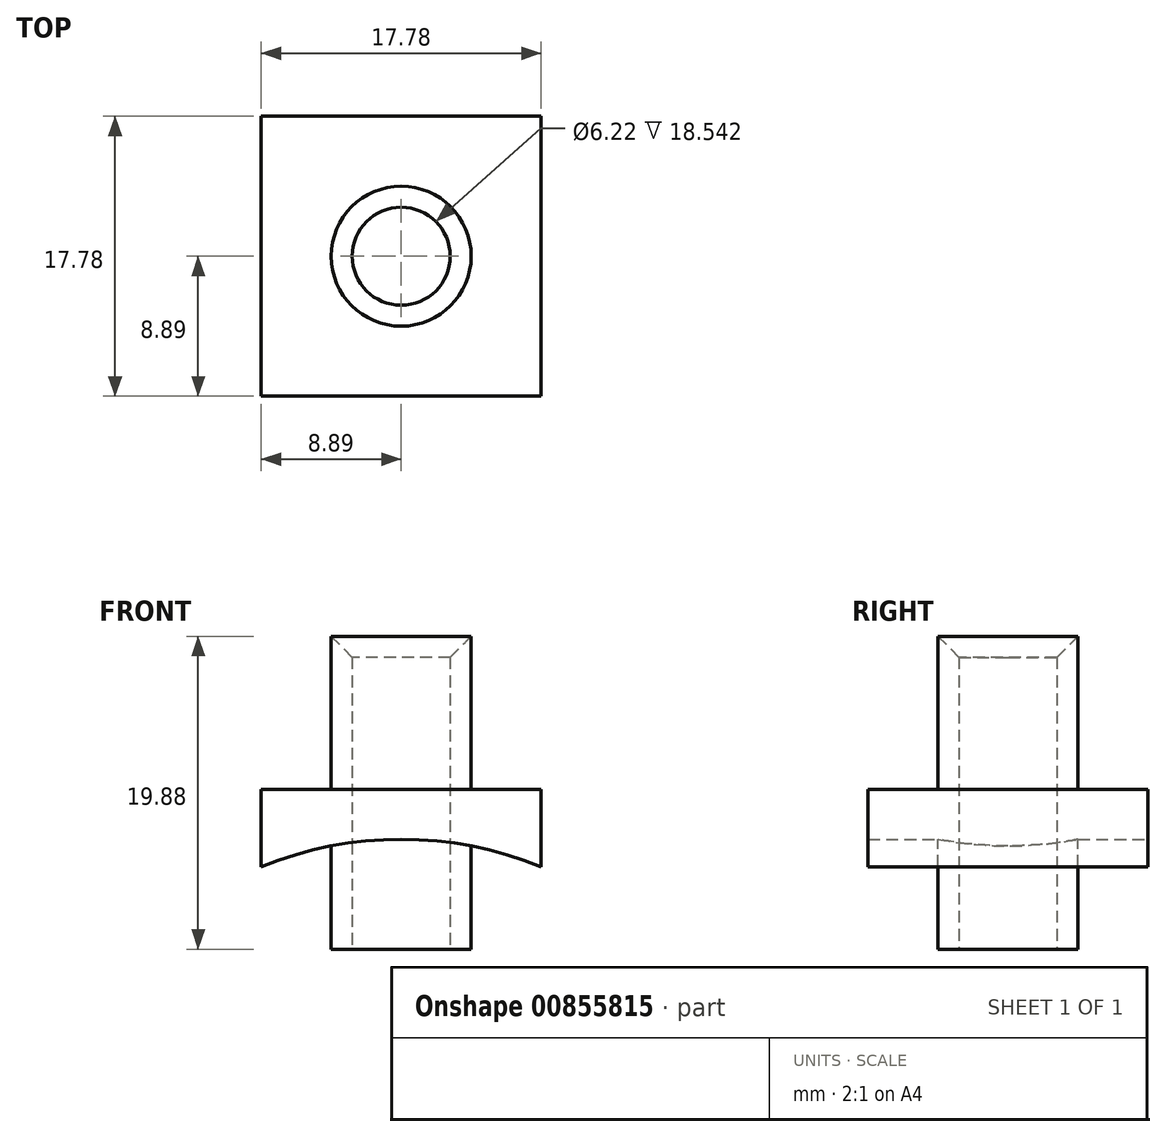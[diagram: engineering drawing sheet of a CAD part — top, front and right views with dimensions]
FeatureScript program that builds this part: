
annotation { "Feature Type Name" : "Feature", "Feature Type Description" : "" }
export const myFeature = defineFeature(function(context is Context, id is Id, definition is map)
    precondition{}
    {
        {
            var Q0;
            Q0=qCreatedBy(makeId("Top.planeOp"),FACE);
            var sketch = newSketch(context, id + "F0", { "sketchPlane" : qUnion([Q0])});
            skLineSegment(sketch, "E0.bottom", {"start": v(0, 17.78) * mm, "end": v(17.78, 17.78) * mm});
            skLineSegment(sketch, "E0.top", {"start": v(0, 0) * mm, "end": v(17.78, 0) * mm});
            skLineSegment(sketch, "E0.left", {"start": v(0, 17.78) * mm, "end": v(0, 0) * mm});
            skLineSegment(sketch, "E0.right", {"start": v(17.78, 17.78) * mm, "end": v(17.78, 0) * mm});
            skSolve(sketch);
        }
        {
            var Q0;
            Q0=makeQuery(id+"F0.imprint","IMPRINT",FACE,{"disambiguationData":[TD([[makeQuery(id+"F0.imprint","IMPRINT",EDGE,{"derivedFrom":sQuery(id+"F0.wireOp",EDGE,"E0.bottom")}),-1.0]])]});
            extrude(context, id + "F1", {"entities" : qUnion([Q0]), "depth" : 7.62 * mm, "offsetDistance" : 25.4 * mm});
        }
        {
            var Q0;
            Q0=makeQuery(id+"F1.opExtrude","CAP_FACE",FACE,{"disambiguationData":[OSD([sQuery(id+"F0.wireOp",EDGE,"E0.bottom"),sQuery(id+"F0.wireOp",EDGE,"E0.top"),sQuery(id+"F0.wireOp",EDGE,"E0.left"),sQuery(id+"F0.wireOp",EDGE,"E0.right")])],"isStart":true});
            cPlane(context, id + "F2", {"entities" : qUnion([Q0]), "cplaneType" : CPlaneType.OFFSET, "offset" : 19.05 * mm, "width" : 152.4 * mm, "height" : 152.4 * mm});
        }
        {
            var Q0;
            Q0=qCreatedBy(id+"F2.planeOp",FACE);
            var sketch = newSketch(context, id + "F3", { "sketchPlane" : qUnion([Q0])});
            skLineSegment(sketch, "E1.bottom", {"start": v(-9.53, 2.47) * mm, "end": v(-14.6, 2.47) * mm});
            skLineSegment(sketch, "E1.top", {"start": v(-9.52, -20.25) * mm, "end": v(-14.6, -20.25) * mm});
            skLineSegment(sketch, "E1.left", {"start": v(-9.53, 2.47) * mm, "end": v(-9.52, -20.25) * mm});
            skLineSegment(sketch, "E1.right", {"start": v(-14.6, 2.47) * mm, "end": v(-14.6, -20.25) * mm});
            skLineSegment(sketch, "E2", {"start": v(8.9, 0) * mm, "end": v(8.9, -24.22) * mm, "construction": true});
            skSolve(sketch);
        }
        {
            var Q0;
            Q0=makeQuery(id+"F3.imprint","IMPRINT",FACE,{"disambiguationData":[TD([[makeQuery(id+"F3.imprint","IMPRINT",EDGE,{"derivedFrom":sQuery(id+"F3.wireOp",EDGE,"E1.bottom")}),1.0]])]});
            var Q1;
            Q1=sQuery(id+"F3.wireOp",EDGE,"E2");
            revolve(context, id + "F4", {"operationType" : NewBodyOperationType.REMOVE, "surfaceOperationType" : NewSurfaceOperationType.NEW, "entities" : qUnion([Q0]), "axis" : qUnion([Q1]), "revolveType" : RevolveType.FULL, "oppositeDirection" : true});
        }
        {
            var Q0;
            Q0=makeQuery(id+"F1.opExtrude","CAP_FACE",FACE,{"disambiguationData":[OSD([sQuery(id+"F0.wireOp",EDGE,"E0.bottom"),sQuery(id+"F0.wireOp",EDGE,"E0.top"),sQuery(id+"F0.wireOp",EDGE,"E0.left"),sQuery(id+"F0.wireOp",EDGE,"E0.right")])],"isStart":false});
            var sketch = newSketch(context, id + "F5", { "sketchPlane" : qUnion([Q0])});
            skCircle(sketch, "E3", {"center": v(8.9, 8.9) * mm, "radius": 4.45 * mm});
            skCircle(sketch, "E4", {"center": v(8.9, 8.9) * mm, "radius": 3.11 * mm});
            skSolve(sketch);
        }
        {
            var Q0;
            Q0=makeQuery(id+"F5.imprint","IMPRINT",FACE,{"disambiguationData":[TD([[makeQuery(id+"F5.imprint","IMPRINT",EDGE,{"derivedFrom":sQuery(id+"F5.wireOp",EDGE,"E3")}),1.0]])]});
            extrude(context, id + "F6", {"entities" : qUnion([Q0]), "operationType" : NewBodyOperationType.ADD, "depth" : 10.16 * mm, "offsetDistance" : 25.4 * mm});
        }
        {
            var Q0;
            Q0=makeQuery(id+"F6.boolean.opBoolean","SPLIT",FACE,{"disambiguationData":[TD([makeQuery(id+"F6.opExtrude","SWEPT_FACE",FACE,{"disambiguationData":[OSD([sQuery(id+"F5.wireOp",EDGE,"E4")])]})])],"derivedFrom":makeQuery(id+"F1.opExtrude","CAP_FACE",FACE,{"disambiguationData":[OSD([sQuery(id+"F0.wireOp",EDGE,"E0.bottom"),sQuery(id+"F0.wireOp",EDGE,"E0.top"),sQuery(id+"F0.wireOp",EDGE,"E0.left"),sQuery(id+"F0.wireOp",EDGE,"E0.right")])],"isStart":false})});
            extrude(context, id + "F7", {"entities" : qUnion([Q0]), "operationType" : NewBodyOperationType.REMOVE, "oppositeDirection" : true, "depth" : 25.4 * mm, "offsetDistance" : 25.4 * mm});
        }
        {
            var Q0;
            Q0 = qSketchRegion(id + "F5", true);
            extrude(context, id + "F8", {"entities" : qUnion([Q0]), "operationType" : NewBodyOperationType.ADD, "oppositeDirection" : true, "depth" : 10.16 * mm, "offsetDistance" : 25.4 * mm});
        }
        {
            var Q0;
            Q0=makeQuery(id+"F6.opExtrude","CAP_EDGE",EDGE,{"disambiguationData":[OSD([sQuery(id+"F5.wireOp",EDGE,"E4")])],"isStart":false});
            chamfer(context, id + "F9", {"entities" : qUnion([Q0]), "width" : 1.78 * mm, "tangentPropagation" : true});
        }
    });
